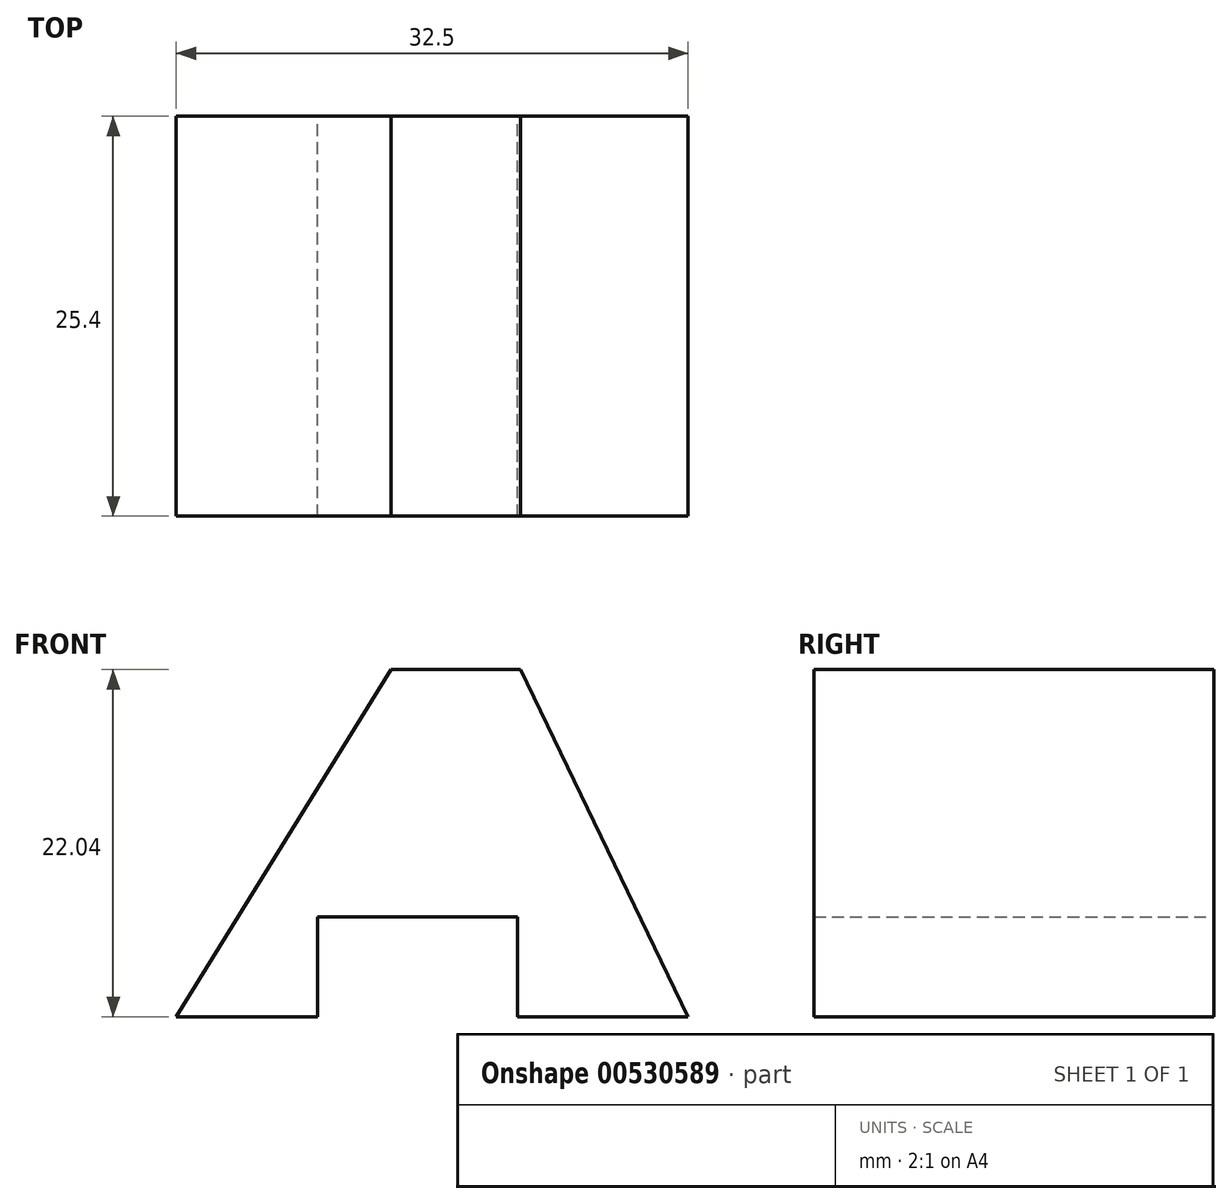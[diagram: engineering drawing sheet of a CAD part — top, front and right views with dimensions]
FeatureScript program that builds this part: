
annotation { "Feature Type Name" : "Feature", "Feature Type Description" : "" }
export const myFeature = defineFeature(function(context is Context, id is Id, definition is map)
    precondition{}
    {
        {
            var Q0;
            Q0=qCreatedBy(makeId("Front.planeOp"),FACE);
            var sketch = newSketch(context, id + "F0", { "sketchPlane" : qUnion([Q0])});
            skLineSegment(sketch, "E0", {"start": v(-48.9, 18.53) * mm, "end": v(-57.86, 18.53) * mm});
            skLineSegment(sketch, "E1", {"start": v(-57.86, 18.53) * mm, "end": v(-44.23, 40.57) * mm});
            skLineSegment(sketch, "E2", {"start": v(-44.23, 40.57) * mm, "end": v(-36.01, 40.57) * mm});
            skLineSegment(sketch, "E3", {"start": v(-48.9, 18.53) * mm, "end": v(-48.9, 24.88) * mm});
            skLineSegment(sketch, "E4", {"start": v(-48.9, 24.88) * mm, "end": v(-36.2, 24.88) * mm});
            skLineSegment(sketch, "E5", {"start": v(-36.2, 24.88) * mm, "end": v(-36.2, 18.53) * mm});
            skLineSegment(sketch, "E6", {"start": v(-36.2, 18.53) * mm, "end": v(-25.36, 18.53) * mm});
            skLineSegment(sketch, "E7", {"start": v(-25.36, 18.53) * mm, "end": v(-36.01, 40.57) * mm});
            skSolve(sketch);
        }
        {
            var Q0;
            Q0=makeQuery(id+"F0.imprint","IMPRINT",FACE,{"disambiguationData":[TD([[makeQuery(id+"F0.imprint","IMPRINT",EDGE,{"derivedFrom":sQuery(id+"F0.wireOp",EDGE,"E0")}),-1.0]])]});
            extrude(context, id + "F1", {"entities" : qUnion([Q0]), "depth" : 25.4 * mm, "offsetDistance" : 25.4 * mm});
        }
    });
